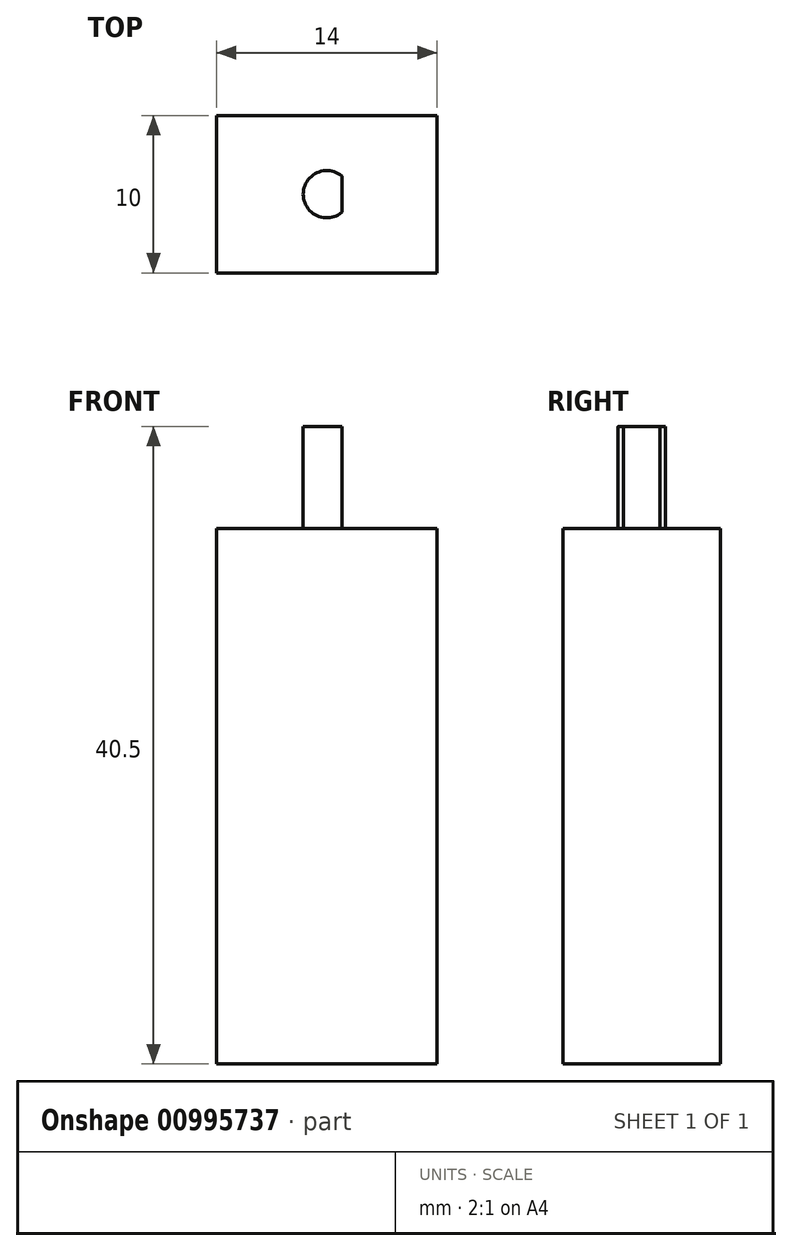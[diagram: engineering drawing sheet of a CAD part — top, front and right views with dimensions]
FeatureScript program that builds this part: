
annotation { "Feature Type Name" : "Feature", "Feature Type Description" : "" }
export const myFeature = defineFeature(function(context is Context, id is Id, definition is map)
    precondition{}
    {
        {
            var Q0;
            Q0=qCreatedBy(makeId("Top.planeOp"),FACE);
            var sketch = newSketch(context, id + "F0", { "sketchPlane" : qUnion([Q0])});
            skLineSegment(sketch, "E0.bottom", {"start": v(7, -5) * mm, "end": v(-7, -5) * mm});
            skLineSegment(sketch, "E0.top", {"start": v(7, 5) * mm, "end": v(-7, 5) * mm});
            skLineSegment(sketch, "E0.left", {"start": v(7, -5) * mm, "end": v(7, 5) * mm});
            skLineSegment(sketch, "E0.right", {"start": v(-7, -5) * mm, "end": v(-7, 5) * mm});
            skPoint(sketch, "E0.middle", {"position": v(0, 0) * mm});
            skSolve(sketch);
        }
        {
            var Q0;
            Q0=makeQuery(id+"F0.imprint","IMPRINT",FACE,{"disambiguationData":[TD([[makeQuery(id+"F0.imprint","IMPRINT",EDGE,{"derivedFrom":sQuery(id+"F0.wireOp",EDGE,"E0.bottom")}),-1.0]])]});
            extrude(context, id + "F1", {"entities" : qUnion([Q0]), "depth" : 34 * mm, "offsetDistance" : 25 * mm});
        }
        {
            var Q0;
            Q0=makeQuery(id+"F1.opExtrude","CAP_FACE",FACE,{"disambiguationData":[OSD([sQuery(id+"F0.wireOp",EDGE,"E0.bottom"),sQuery(id+"F0.wireOp",EDGE,"E0.top"),sQuery(id+"F0.wireOp",EDGE,"E0.left"),sQuery(id+"F0.wireOp",EDGE,"E0.right")])],"isStart":false});
            var sketch = newSketch(context, id + "F2", { "sketchPlane" : qUnion([Q0])});
            skArc(sketch, "E1", {"start": v(0.97, 1.15) * mm, "mid": v(-1.5, 0) * mm, "end": v(0.97, -1.15) * mm});
            skLineSegment(sketch, "E2", {"start": v(0.97, 1.15) * mm, "end": v(0.97, -1.15) * mm});
            skSolve(sketch);
        }
        {
            var Q0;
            Q0=makeQuery(id+"F2.imprint","IMPRINT",FACE,{"disambiguationData":[TD([[makeQuery(id+"F2.imprint","IMPRINT",EDGE,{"derivedFrom":sQuery(id+"F2.wireOp",EDGE,"E1")}),1.0]])]});
            extrude(context, id + "F3", {"entities" : qUnion([Q0]), "operationType" : NewBodyOperationType.ADD, "depth" : 6.5 * mm, "offsetDistance" : 25 * mm});
        }
    });
